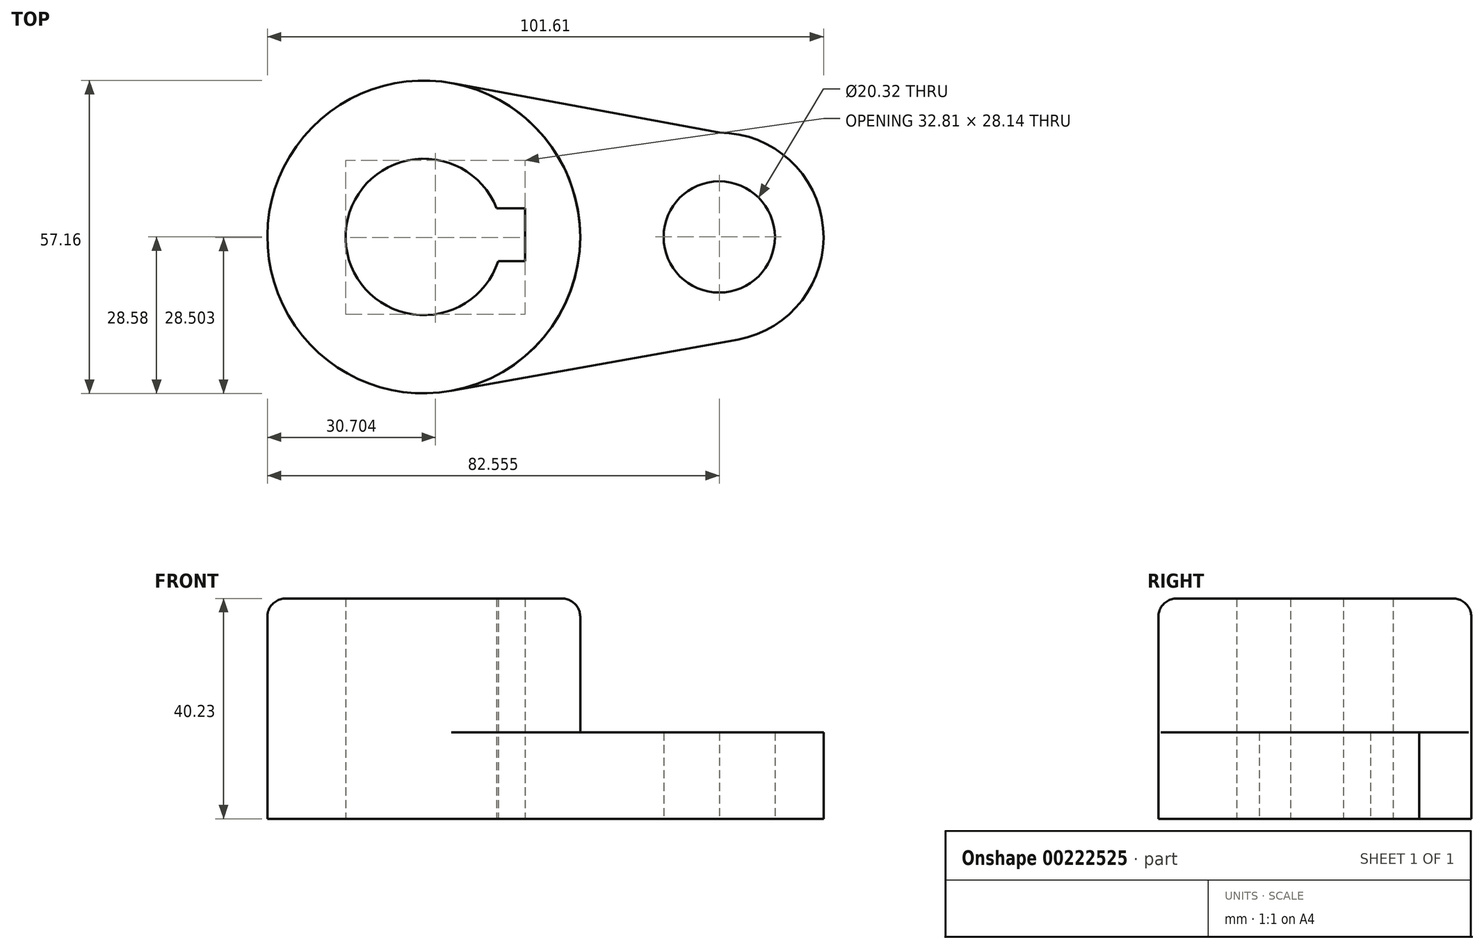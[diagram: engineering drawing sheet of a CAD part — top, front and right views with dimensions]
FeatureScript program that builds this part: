
annotation { "Feature Type Name" : "Feature", "Feature Type Description" : "" }
export const myFeature = defineFeature(function(context is Context, id is Id, definition is map)
    precondition{}
    {
        {
            var Q0;
            Q0=qCreatedBy(makeId("Top.planeOp"),FACE);
            var sketch = newSketch(context, id + "F0", { "sketchPlane" : qUnion([Q0])});
            skArc(sketch, "E0", {"start": v(13.29, 5.25) * mm, "mid": v(-14.28, -0.45) * mm, "end": v(13.6, -4.4) * mm});
            skCircle(sketch, "E1", {"center": v(0, 0) * mm, "radius": 28.58 * mm});
            skLineSegment(sketch, "E2.bottom", {"start": v(13.29, 5.25) * mm, "end": v(18.53, 5.25) * mm});
            skLineSegment(sketch, "E2.top", {"start": v(13.6, -4.4) * mm, "end": v(18.53, -4.4) * mm});
            skLineSegment(sketch, "E2.right", {"start": v(18.53, 5.25) * mm, "end": v(18.53, -4.4) * mm});
            skLineSegment(sketch, "E3", {"start": v(0, 0) * mm, "end": v(53.98, 0) * mm, "construction": true});
            skCircle(sketch, "E4", {"center": v(53.98, 0) * mm, "radius": 10.16 * mm});
            skArc(sketch, "E5", {"start": v(57.34, -18.75) * mm, "mid": v(72.95, 1.69) * mm, "end": v(53.98, 19.05) * mm});
            skLineSegment(sketch, "E6", {"start": v(53.98, 19.05) * mm, "end": v(5.21, 28.1) * mm});
            skLineSegment(sketch, "E7", {"start": v(57.34, -18.75) * mm, "end": v(5.04, -28.13) * mm});
            skSolve(sketch);
        }
        {
            var Q0;
            Q0=makeQuery(id+"F0.imprint","IMPRINT",FACE,{"disambiguationData":[TD([[makeQuery(id+"F0.imprint","IMPRINT",EDGE,{"derivedFrom":sQuery(id+"F0.wireOp",EDGE,"E0")}),-1.0]])]});
            extrude(context, id + "F1", {"entities" : qUnion([Q0]), "depth" : 40.23 * mm});
        }
        {
            var Q0;
            Q0=makeQuery(id+"F0.imprint","IMPRINT",FACE,{"disambiguationData":[TD([[makeQuery(id+"F0.imprint","IMPRINT",EDGE,{"derivedFrom":sQuery(id+"F0.wireOp",EDGE,"E4")}),-1.0]])]});
            extrude(context, id + "F2", {"entities" : qUnion([Q0]), "operationType" : NewBodyOperationType.ADD, "depth" : 15.77 * mm});
        }
        {
            var Q0;
            Q0=makeQuery(id+"F1.opExtrude","CAP_EDGE",EDGE,{"disambiguationData":[OSD([sQuery(id+"F0.wireOp",EDGE,"E1")])],"isStart":false});
            fillet(context, id + "F3", {"entities" : qUnion([Q0]), "radius" : 3.3 * mm, "tangentPropagation" : true, "allowEdgeOverflow" : false});
        }
    });
